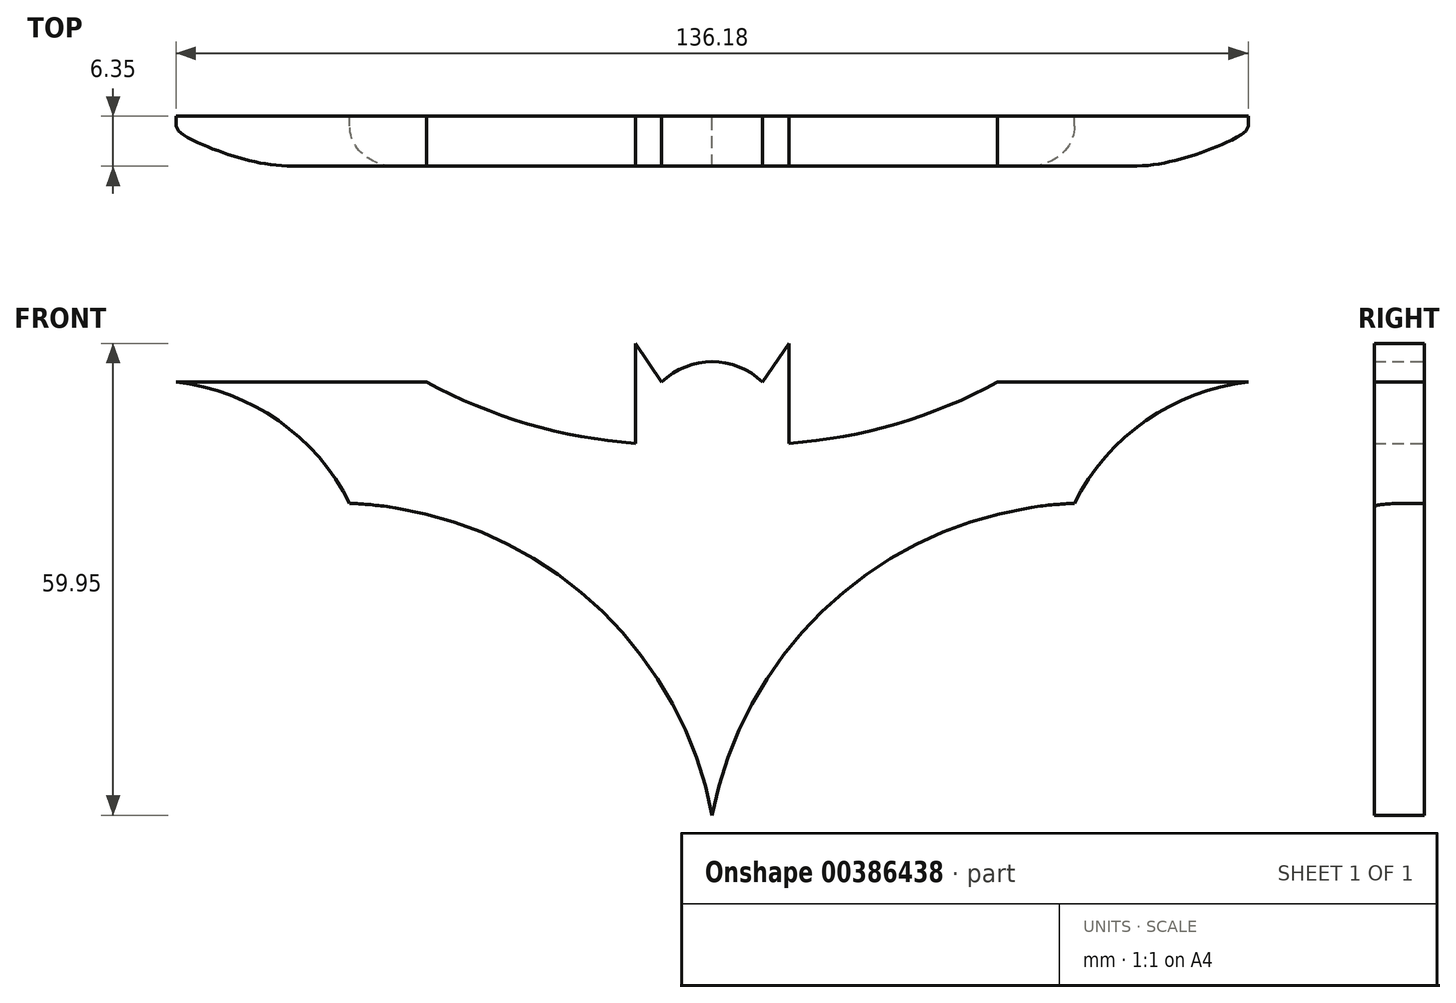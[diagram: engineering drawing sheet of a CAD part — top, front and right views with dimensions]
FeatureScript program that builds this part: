
annotation { "Feature Type Name" : "Feature", "Feature Type Description" : "" }
export const myFeature = defineFeature(function(context is Context, id is Id, definition is map)
    precondition{}
    {
        {
            var Q0;
            Q0=qCreatedBy(makeId("Front.planeOp"),FACE);
            var sketch = newSketch(context, id + "F0", { "sketchPlane" : qUnion([Q0])});
            skArc(sketch, "E0", {"start": v(46.02, -15.4) * mm, "mid": v(16.1, -27.18) * mm, "end": v(0, -55.02) * mm});
            skArc(sketch, "E1.MirrorCS", {"start": v(-46.02, -15.4) * mm, "mid": v(-16.1, -27.18) * mm, "end": v(0, -55.02) * mm});
            skArc(sketch, "E2", {"start": v(-46.02, -15.4) * mm, "mid": v(-57.78, -3.24) * mm, "end": v(-74.37, 0) * mm});
            skArc(sketch, "E3.MirrorCS", {"start": v(46.02, -15.4) * mm, "mid": v(57.78, -3.24) * mm, "end": v(74.37, 0) * mm});
            skLineSegment(sketch, "E4", {"start": v(-74.37, 0) * mm, "end": v(-36.27, 0) * mm});
            skLineSegment(sketch, "E5.MirrorCS", {"start": v(74.37, 0) * mm, "end": v(36.27, 0) * mm});
            skArc(sketch, "E6", {"start": v(-36.27, 0) * mm, "mid": v(-23.42, -5.3) * mm, "end": v(-9.75, -7.77) * mm});
            skArc(sketch, "E7.MirrorCS", {"start": v(36.27, 0) * mm, "mid": v(23.42, -5.3) * mm, "end": v(9.75, -7.77) * mm});
            skLineSegment(sketch, "E8", {"start": v(-9.75, -7.77) * mm, "end": v(-9.75, 4.93) * mm});
            skLineSegment(sketch, "E9.MirrorCS", {"start": v(9.75, -7.77) * mm, "end": v(9.75, 4.93) * mm});
            skLineSegment(sketch, "E10", {"start": v(-9.75, 4.93) * mm, "end": v(-6.4, 0) * mm});
            skLineSegment(sketch, "E11.MirrorCS", {"start": v(9.75, 4.93) * mm, "end": v(6.4, 0) * mm});
            skArc(sketch, "E12", {"start": v(6.4, 0) * mm, "mid": v(0, 2.6) * mm, "end": v(-6.4, 0) * mm});
            skSolve(sketch);
        }
        {
            var Q0;
            {var subQ8=sQuery(id+"F0.wireOp",EDGE,"E0");Q0=makeQuery(id+"F0.imprint","IMPRINT",FACE,{"disambiguationData":[TD([[makeQuery(id+"F0.imprint","IMPRINT",EDGE,{"derivedFrom":subQ8}),-1.0]])]});}
            extrude(context, id + "F1", {"entities" : qUnion([Q0]), "depth" : 6.35 * mm});
        }
        {
            var Q0;
            Q0=makeQuery(id+"F1.opExtrude","CAP_EDGE",EDGE,{"disambiguationData":[OSD([sQuery(id+"F0.wireOp",EDGE,"E2")])],"isStart":false});
            fillet(context, id + "F2", {"entities" : qUnion([Q0]), "radius" : 5.08 * mm, "tangentPropagation" : true, "allowEdgeOverflow" : false});
        }
        {
            var Q0;
            Q0=makeQuery(id+"F1.opExtrude","CAP_EDGE",EDGE,{"disambiguationData":[OSD([sQuery(id+"F0.wireOp",EDGE,"E3.MirrorCS")])],"isStart":false});
            fillet(context, id + "F3", {"entities" : qUnion([Q0]), "radius" : 5.08 * mm, "tangentPropagation" : true, "allowEdgeOverflow" : false});
        }
    });
